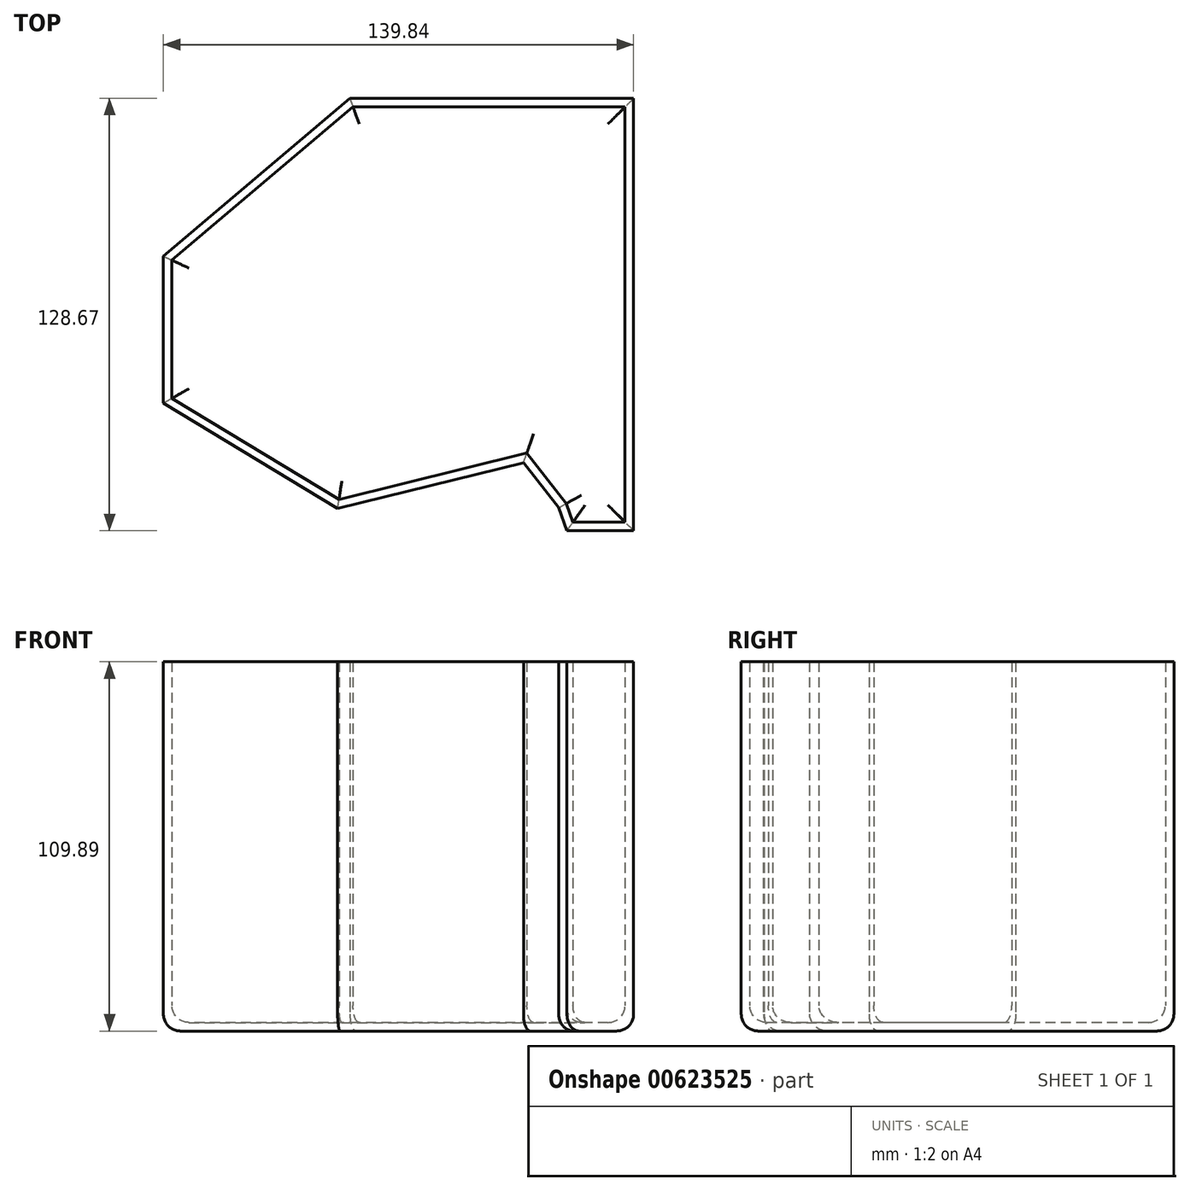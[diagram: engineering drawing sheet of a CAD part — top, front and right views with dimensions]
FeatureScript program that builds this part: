
annotation { "Feature Type Name" : "Feature", "Feature Type Description" : "" }
export const myFeature = defineFeature(function(context is Context, id is Id, definition is map)
    precondition{}
    {
        {
            var Q0;
            Q0=qCreatedBy(makeId("Top.planeOp"),FACE);
            var sketch = newSketch(context, id + "F0", { "sketchPlane" : qUnion([Q0])});
            skLineSegment(sketch, "E0.bottom", {"start": v(84.85, 69.05) * mm, "end": v(-55, 69.05) * mm});
            skLineSegment(sketch, "E0.top", {"start": v(84.85, -59.62) * mm, "end": v(-55, -59.62) * mm});
            skLineSegment(sketch, "E0.left", {"start": v(84.85, 69.05) * mm, "end": v(84.85, -59.62) * mm});
            skLineSegment(sketch, "E0.right", {"start": v(-55, 69.05) * mm, "end": v(-55, -59.62) * mm});
            skLineSegment(sketch, "E1", {"start": v(0.46, 69.05) * mm, "end": v(-55, 22.05) * mm});
            skLineSegment(sketch, "E2", {"start": v(-55, 22.05) * mm, "end": v(-55, -21.63) * mm});
            skLineSegment(sketch, "E3", {"start": v(-55, -21.63) * mm, "end": v(-3.18, -53.02) * mm});
            skLineSegment(sketch, "E4", {"start": v(-3.18, -53.02) * mm, "end": v(52.1, -39.37) * mm});
            skLineSegment(sketch, "E5", {"start": v(52.1, -39.37) * mm, "end": v(62.56, -52.79) * mm});
            skLineSegment(sketch, "E6", {"start": v(62.56, -52.79) * mm, "end": v(65.51, -60.98) * mm});
            skSolve(sketch);
        }
        {
            var Q0;
            {var subQ0=sQuery(id+"F0.wireOp",EDGE,"E0.left");Q0=makeQuery(id+"F0.imprint","IMPRINT",FACE,{"disambiguationData":[TD([[makeQuery(id+"F0.imprint","IMPRINT",EDGE,{"derivedFrom":subQ0}),-1.0]])]});}
            extrude(context, id + "F1", {"entities" : qUnion([Q0]), "depth" : 109.89 * mm, "offsetDistance" : 25.4 * mm});
        }
        {
            var Q0;
            Q0=makeQuery(id+"F1.opExtrude","CAP_FACE",FACE,{"disambiguationData":[OSD([sQuery(id+"F0.wireOp",EDGE,"E0.bottom"),sQuery(id+"F0.wireOp",EDGE,"E0.top"),sQuery(id+"F0.wireOp",EDGE,"E0.left"),sQuery(id+"F0.wireOp",EDGE,"E1"),sQuery(id+"F0.wireOp",EDGE,"E2"),sQuery(id+"F0.wireOp",EDGE,"E3"),sQuery(id+"F0.wireOp",EDGE,"E4"),sQuery(id+"F0.wireOp",EDGE,"E5"),sQuery(id+"F0.wireOp",EDGE,"E6")])],"isStart":false});
            shell(context, id + "F2", {"entities" : qUnion([Q0]), "thickness" : 2.54 * mm});
        }
        {
            var Q0;
            Q0=makeQuery(id+"F2.opShell","OFFSET_FACE",FACE,{"disambiguationData":[OSD([sQuery(id+"F0.wireOp",EDGE,"E0.bottom"),sQuery(id+"F0.wireOp",EDGE,"E0.top"),sQuery(id+"F0.wireOp",EDGE,"E0.left"),sQuery(id+"F0.wireOp",EDGE,"E1"),sQuery(id+"F0.wireOp",EDGE,"E2"),sQuery(id+"F0.wireOp",EDGE,"E3"),sQuery(id+"F0.wireOp",EDGE,"E4"),sQuery(id+"F0.wireOp",EDGE,"E5"),sQuery(id+"F0.wireOp",EDGE,"E6")])]});
            fillet(context, id + "F3", {"entities" : qUnion([Q0]), "radius" : 5.08 * mm, "tangentPropagation" : true, "allowEdgeOverflow" : false});
        }
        {
            var Q0;
            Q0=makeQuery(id+"F1.opExtrude","CAP_FACE",FACE,{"disambiguationData":[OSD([sQuery(id+"F0.wireOp",EDGE,"E0.bottom"),sQuery(id+"F0.wireOp",EDGE,"E0.top"),sQuery(id+"F0.wireOp",EDGE,"E0.left"),sQuery(id+"F0.wireOp",EDGE,"E1"),sQuery(id+"F0.wireOp",EDGE,"E2"),sQuery(id+"F0.wireOp",EDGE,"E3"),sQuery(id+"F0.wireOp",EDGE,"E4"),sQuery(id+"F0.wireOp",EDGE,"E5"),sQuery(id+"F0.wireOp",EDGE,"E6")])],"isStart":true});
            fillet(context, id + "F4", {"entities" : qUnion([Q0]), "radius" : 5.08 * mm, "tangentPropagation" : true, "allowEdgeOverflow" : false});
        }
    });
